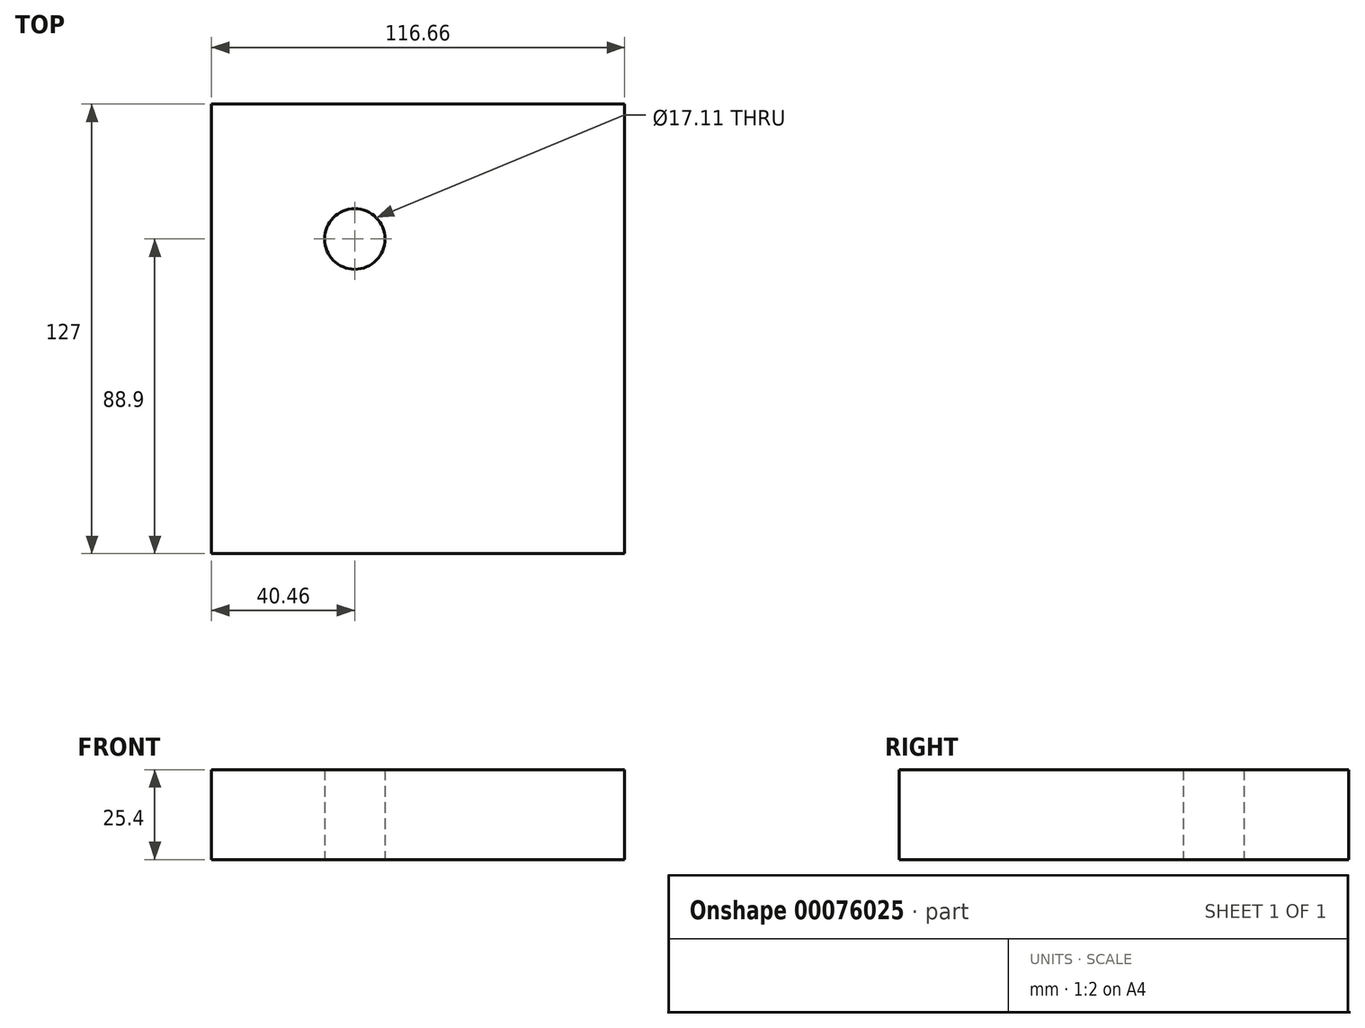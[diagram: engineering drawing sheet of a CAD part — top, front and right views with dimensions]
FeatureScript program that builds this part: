
annotation { "Feature Type Name" : "Feature", "Feature Type Description" : "" }
export const myFeature = defineFeature(function(context is Context, id is Id, definition is map)
    precondition{}
    {
        {
            var Q0;
            Q0=qCreatedBy(makeId("Top.planeOp"),FACE);
            var sketch = newSketch(context, id + "F0", { "sketchPlane" : qUnion([Q0])});
            skLineSegment(sketch, "E0", {"start": v(-40.46, -88.9) * mm, "end": v(76.2, -88.9) * mm});
            skLineSegment(sketch, "E1", {"start": v(76.2, -88.9) * mm, "end": v(76.2, 38.1) * mm});
            skLineSegment(sketch, "E2", {"start": v(76.2, 38.1) * mm, "end": v(-40.46, 38.1) * mm});
            skLineSegment(sketch, "E3", {"start": v(-40.46, 38.1) * mm, "end": v(-40.46, -88.9) * mm});
            skCircle(sketch, "E4", {"center": v(0, 0) * mm, "radius": 8.56 * mm});
            skSolve(sketch);
        }
        {
            var Q0;
            Q0=makeQuery(id+"F0.imprint","IMPRINT",FACE,{"disambiguationData":[TD([[makeQuery(id+"F0.imprint","IMPRINT",EDGE,{"derivedFrom":sQuery(id+"F0.wireOp",EDGE,"E0")}),1.0]])]});
            extrude(context, id + "F1", {"entities" : qUnion([Q0]), "endBound" : BoundingType.SYMMETRIC, "depth" : 25.4 * mm});
        }
    });
